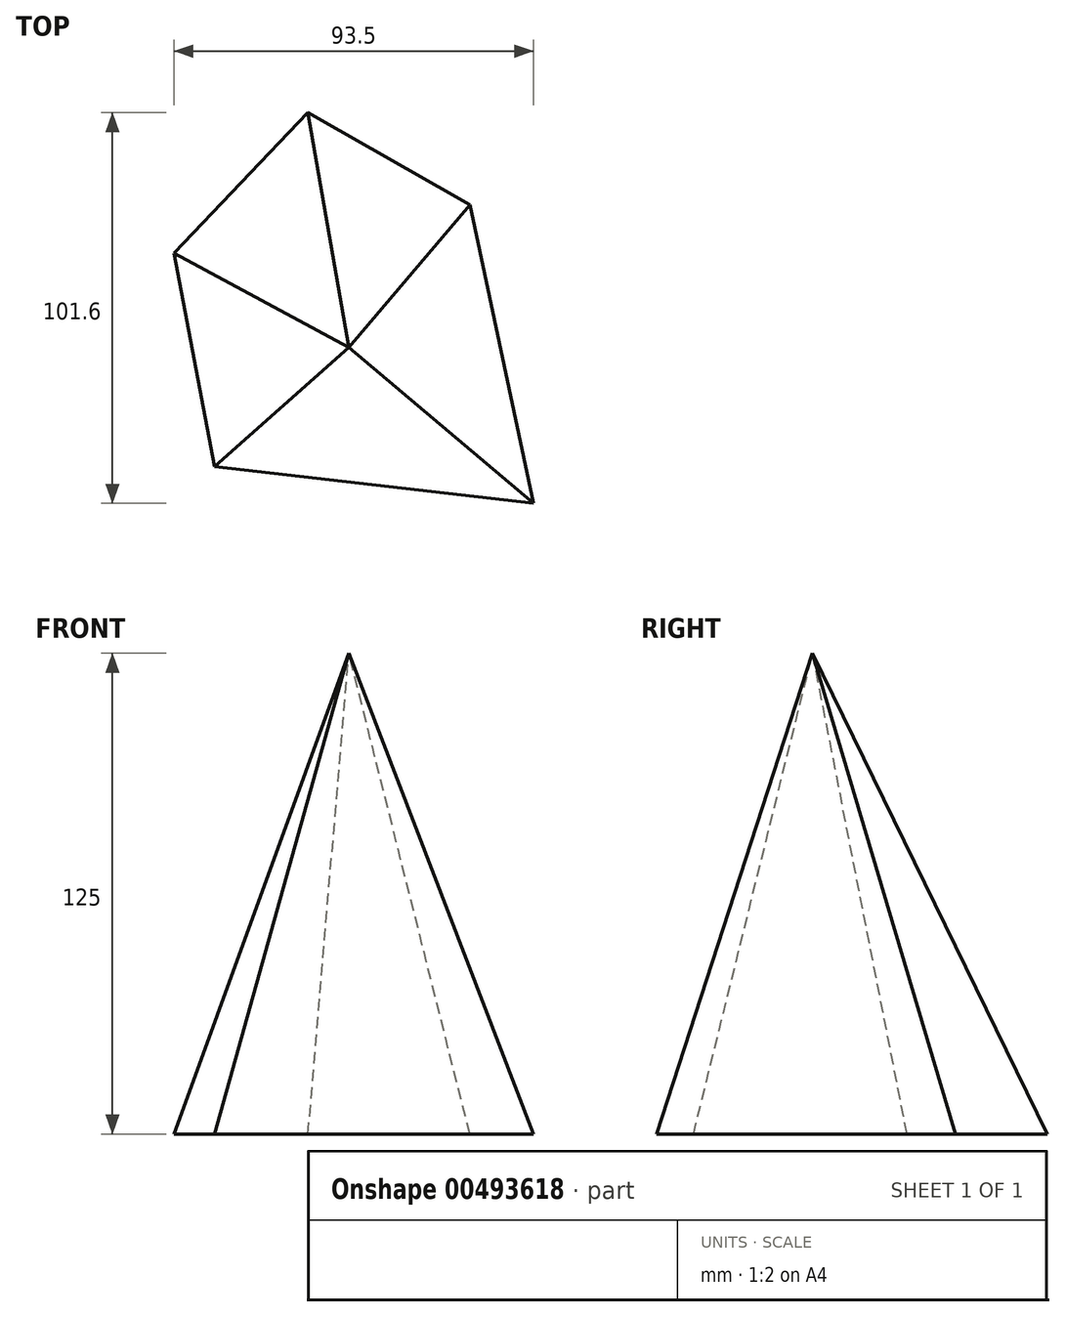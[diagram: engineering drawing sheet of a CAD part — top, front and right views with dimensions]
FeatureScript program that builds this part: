
annotation { "Feature Type Name" : "Feature", "Feature Type Description" : "" }
export const myFeature = defineFeature(function(context is Context, id is Id, definition is map)
    precondition{}
    {
        {
            var Q0;
            Q0=qCreatedBy(makeId("Top.planeOp"),FACE);
            var sketch = newSketch(context, id + "F0", { "sketchPlane" : qUnion([Q0])});
            skLineSegment(sketch, "E0", {"start": v(-34.97, -30.97) * mm, "end": v(-45.47, 24.55) * mm});
            skLineSegment(sketch, "E1", {"start": v(-45.47, 24.55) * mm, "end": v(-10.63, 61.08) * mm});
            skLineSegment(sketch, "E2", {"start": v(-10.63, 61.08) * mm, "end": v(31.42, 37.13) * mm});
            skLineSegment(sketch, "E3", {"start": v(31.42, 37.13) * mm, "end": v(48.03, -40.52) * mm});
            skLineSegment(sketch, "E4", {"start": v(-34.97, -30.97) * mm, "end": v(48.03, -40.52) * mm});
            skSolve(sketch);
        }
        {
            var Q0;
            Q0=qCreatedBy(makeId("Top.planeOp"),FACE);
            cPlane(context, id + "F1", {"entities" : qUnion([Q0]), "cplaneType" : CPlaneType.OFFSET, "offset" : 125 * mm, "width" : 150 * mm, "height" : 150 * mm});
        }
        {
            var Q0;
            Q0=qCreatedBy(id+"F1.planeOp",FACE);
            var sketch = newSketch(context, id + "F2", { "sketchPlane" : qUnion([Q0])});
            skPoint(sketch, "E5", {"position": v(0, 0) * mm});
            skSolve(sketch);
        }
        {
            var Q0;
            Q0=makeQuery(id+"F0.imprint","IMPRINT",FACE,{"disambiguationData":[TD([[makeQuery(id+"F0.imprint","IMPRINT",EDGE,{"derivedFrom":sQuery(id+"F0.wireOp",EDGE,"E0")}),-1.0]])]});
            var Q1;
            Q1=sQuery(id+"F2.wireOp",VERTEX,"E5");
            loft(context, id + "F3", {"sheetProfilesArray" : [{ "sheetProfileEntities" : qUnion([Q0]) }, { "sheetProfileEntities" : qUnion([Q1]) }]});
        }
    });
